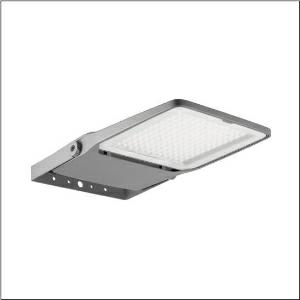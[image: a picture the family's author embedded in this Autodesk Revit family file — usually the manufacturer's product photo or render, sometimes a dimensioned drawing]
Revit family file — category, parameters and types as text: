
# Revit family: floodlight_fl_20_midi___pl52_5xa7682d1d2ac_d798
name_source: partatom
category: Lighting Fixtures
units: mm (PartAtom-declared; Revit-internal decimal feet)

## family parameters
Cut with Voids When Loaded = No
Host = Face
Light Source = No
Part Type = Normal
Room Calculation Point = No
Round Connector Dimension = Use Diameter
Shared = No

## types (1)
- --- (1 x LED 3000K / CRI = 80 (unbekannt), 14130 lm, 3000K)
    Apparent Load = 142 VA
    CIE Flux Codes = 27 59 98 100 100
    Color Rendering = 80
    Color Temperature = 3000K
    Default Elevation = 1800 mm
    Description = Floodlight FL 20 midi, floodlight, primary light control with lens, of plastic, primary optical cover: protective disc, of toughened safety glass, transparent, light distribution: PL52, light emission: direct distribution, primary light characteristic: asymmetric, installation type: surface-mounted, LED High Power LED, rated luminous flux: 14.130 lm, light colour: 830, colour temperature: 3000K, control gear: ECG Plus, control: flexible luminous flux parameterisation, time-dependent luminous flux control, digital communication interface, power reduction, overheat protection, electronic power reduction, with terminal, 5-pole, max. 2.5mm², mains connection: 220..240V, AC, 50/60Hz, rated input power: 142W, LED unit, of diecast aluminium, powder-coated, Siteco® metallic grey (DB 702S), length: 731 mm, width: 450 mm, height: 76mm, housing frame, of diecast aluminium, powder-coated, Siteco® metallic grey (DB 702S), wall fastening, of steel, powder-coated, Siteco® metallic grey (DB 702S), DALIprotection rating (complete): IP66, insulation class (complete): insulation class II (safety insulation), certification: CE, ENEC, VDE, protection symbol: D, permissible ambient temperature for indoor applications: -40..+40°C, permissible ambient temperature for outdoor applications: -40..+50°C, standard: DIN EN 12944, packaging unit: 1 piece

Light Distribution: PL52
    Height = 76 mm
    Lamp = 1 x LED 3000K / CRI >= 80 (unbekannt)
    Lamp Light Flux = 14130 lm
    Lamp count = 1
    Length = 731 mm
    Luminous efficacy = 100 lm/W
    Manufacturer = Siteco
    ModVariant = No
    Model = 5XA7682D1D2AC
    Number of Poles = 1
    OnlyDefault = Yes
    Power Factor = 1
    Product Name = Floodlight FL 20 midi | PL52
    Product group = floodlight | pylon top
    ProductGroupID = 6101
    Protection Class = Protection class II
    Protection Degree = IP 66
    RLX_Detail_Level = 1
    RlxData = <blob elided: 92045 chars, md5=bf34c2e7>
    Socket = socket
    Standby Power = 0 W
    System Light Flux = 14130 lm
    System Power = 142 W
    Type Comments = factory setting: luminous flux: 100 % | dim-lin: 254 | 489 mA
    Type Image = l_1005944.jpg
    URL = http://relux.com
    VarID = @adj_143369
    Voltage = 0 V
    Weight = 0.00 kg
    Width = 450 mm

## geometry (parser evidence)
native form markers: Blend x4, Sweep x14
no freeform markers — native parametric forms only
